# Revit family: HARMANN-Wentylator-Harmann-ML-EC-R_Wywiewny
name_source: partatom
category: Wyposażenie mechaniczne
units: mm (PartAtom-declared; Revit-internal decimal feet)

## family parameters
Oparty na płaszczyźnie roboczej = Nie
Punkt obliczania pomieszczeń = Nie
Tnij formami wycięć po wczytaniu = Nie
Typ części = Dzieli na
Współdzielony = Nie
Wymiar okrągłego złącza = Użyj średnicy
Zachowaj orientację opisów = Nie
Zawsze pionowo = Tak

## types (6) — shared parameters
Domyślna rzędna = 0.0 mm
IfcExportAs = IfcFanType
IfcExportType = NOTDEFINED
Kod Producent = Harmann
Kod Typoszereg = ML EC.R
Object Date = 2018.11.30
Object Destination = PL
Object ID = F000054RFAPL
Object Language = PL
Object Revit = 2017
Object Version = 1.00
Opis = Kanałowy wentylator  EC z wbudowanym potencjometrem
Otoczenie Temperatura Maksymalna = 50.0 °C
Otoczenie Temperatura Minimalna = -20.0 °C
Powietrze Wywiewane Temperatura Maksymalna = 50.0 °C
Producent = Harmann Polska Sp. z o.o.
Producent Nazwa = Harmann Polska Sp. z o.o.
Systematyka Branża = Instalacje Sanitarne
Systematyka Dziedzina = Instalacje Wentylacyjne
Systematyka Klasa = Wentylator
Systematyka Rodzaj = Wentylator Kanałowy
Zasilanie Częstotliwość Nominalna = 50 Hz
Zasilanie Ilość Faz = 1
Zasilanie Konfiguracja Uzwojeń = n/d
Zasilanie Napięcie Nominalne = 230 V
wx_a0 = 0.0 mm
wy_a0 = 53.9 mm

## per-type parameters (varying)
- ML EC.R 100/280: Kod Numer Katalogowy=01002801; Kod Zamówienia=ML EC.R 100/280; Masa Netto=2.0 kg; Model=ML EC.R 100/280; Opis indeksowy=ML EC.R 100/280; Otoczenie Poziom Ciśnienia Akustycznego Nominalny z 01 m=38; Otoczenie Poziom Ciśnienia Akustycznego Nominalny z 03 m=35; Otoczenie Poziom Mocy Akustycznej Nominalny Obudowa=42; Powietrze Wywiewane Ciśnienie Statyczne Maksymalne=160.0 Pa; Powietrze Wywiewane Ciśnienie Statyczne Nominalne=60.0 Pa; Powietrze Wywiewane Poziom Mocy Akustycznej Nominalny Wlot=52; Powietrze Wywiewane Poziom Mocy Akustycznej Nominalny Wylot=53; Powietrze Wywiewane Przepływ Maksymalny=280 m³/h; Powietrze Wywiewane Przepływ Nominalny=150 m³/h; Prt Komponent N1=GE-Komponent-ParaForma-Harmann-ML-N1a : ML EC.R 100/280; Prt Komponent N2=GE-Komponent-ParaForma-Harmann-ML-N2a : 100/280; Zasilanie Moc=20 W; Zasilanie Moc Pozorna=58 VA; Zasilanie Natężenie=0 A; Zasilanie Rodzaj Sterowania=Sterowanie napięciem 0-10V. Wbudowany potencjometr.; Zasilanie Współczynnik Mocy=0.35; dn=100.0 mm; l1_a0=119.0 mm; l2_a0=119.0 mm; s1=100.0 mm; wz_a0=88.5 mm
- ML EC.R 125/300: Kod Numer Katalogowy=01253001; Kod Zamówienia=ML EC.R 125/300; Masa Netto=1.8 kg; Model=ML EC.R 125/300; Opis indeksowy=ML EC.R 125/300; Otoczenie Poziom Ciśnienia Akustycznego Nominalny z 01 m=37; Otoczenie Poziom Ciśnienia Akustycznego Nominalny z 03 m=34; Otoczenie Poziom Mocy Akustycznej Nominalny Obudowa=41; Powietrze Wywiewane Ciśnienie Statyczne Maksymalne=140.0 Pa; Powietrze Wywiewane Ciśnienie Statyczne Nominalne=50.0 Pa; Powietrze Wywiewane Poziom Mocy Akustycznej Nominalny Wlot=55; Powietrze Wywiewane Poziom Mocy Akustycznej Nominalny Wylot=55; Powietrze Wywiewane Przepływ Maksymalny=300 m³/h; Powietrze Wywiewane Przepływ Nominalny=200 m³/h; Prt Komponent N1=GE-Komponent-ParaForma-Harmann-ML-N1a : ML EC.R 125/300; Prt Komponent N2=GE-Komponent-ParaForma-Harmann-ML-N2a : 125/300; Zasilanie Moc=18 W; Zasilanie Moc Pozorna=61 VA; Zasilanie Natężenie=0 A; Zasilanie Rodzaj Sterowania=Sterowanie napięciem 0-10V. Wbudowany potencjometr.; Zasilanie Współczynnik Mocy=0.21; dn=125.0 mm; l1_a0=99.5 mm; l2_a0=99.5 mm; s1=125.0 mm; wz_a0=88.5 mm
- ML EC.R 150-160/530: Kod Numer Katalogowy=01505301; Kod Zamówienia=ML EC.R 150-160/550; Masa Netto=2.7 kg; Model=ML EC.R 150-160/550; Opis indeksowy=ML EC.R 150-160/550; Otoczenie Poziom Ciśnienia Akustycznego Nominalny z 01 m=439; Otoczenie Poziom Ciśnienia Akustycznego Nominalny z 03 m=36; Otoczenie Poziom Mocy Akustycznej Nominalny Obudowa=43; Powietrze Wywiewane Ciśnienie Statyczne Maksymalne=350.0 Pa; Powietrze Wywiewane Ciśnienie Statyczne Nominalne=80.0 Pa; Powietrze Wywiewane Poziom Mocy Akustycznej Nominalny Wlot=55; Powietrze Wywiewane Poziom Mocy Akustycznej Nominalny Wylot=58; Powietrze Wywiewane Przepływ Maksymalny=530 m³/h; Powietrze Wywiewane Przepływ Nominalny=350 m³/h; Prt Komponent N1=GE-Komponent-ParaForma-Harmann-ML-N1a : ML EC.R 150-160/530; Prt Komponent N2=GE-Komponent-ParaForma-Harmann-ML-N2a : 150-160/530; Zasilanie Moc=50 W; Zasilanie Moc Pozorna=80 VA; Zasilanie Natężenie=0 A; Zasilanie Rodzaj Sterowania=Sterowanie napięciem 0-10V. Wbudowanz potencjometr; Zasilanie Współczynnik Mocy=0.62; dn=160.0 mm; l1_a0=145.0 mm; l2_a0=145.0 mm; s1=160.0 mm; wz_a0=99.5 mm
- ML EC.R 200/1150: Kod Numer Katalogowy=02001151; Kod Zamówienia=ML EC.R 200/950; Masa Netto=4.3 kg; Model=ML EC.R 200/950; Opis indeksowy=ML EC.R 200/950; Otoczenie Poziom Ciśnienia Akustycznego Nominalny z 01 m=44; Otoczenie Poziom Ciśnienia Akustycznego Nominalny z 03 m=41; Otoczenie Poziom Mocy Akustycznej Nominalny Obudowa=48; Powietrze Wywiewane Ciśnienie Statyczne Maksymalne=450.0 Pa; Powietrze Wywiewane Ciśnienie Statyczne Nominalne=100.0 Pa; Powietrze Wywiewane Poziom Mocy Akustycznej Nominalny Wlot=60; Powietrze Wywiewane Poziom Mocy Akustycznej Nominalny Wylot=62; Powietrze Wywiewane Przepływ Maksymalny=1100 m³/h; Powietrze Wywiewane Przepływ Nominalny=700 m³/h; Prt Komponent N1=GE-Komponent-ParaForma-Harmann-ML-N1a : ML EC.R 200/1150; Prt Komponent N2=GE-Komponent-ParaForma-Harmann-ML-N2a : 200/1150; Zasilanie Moc=165 W; Zasilanie Moc Pozorna=241 VA; Zasilanie Natężenie=1 A; Zasilanie Rodzaj Sterowania=Sterowanie napięciem 0-10V. Wbudowany potencjometr.; Zasilanie Współczynnik Mocy=0.68; dn=200.0 mm; l1_a0=120.0 mm; l2_a0=120.0 mm; s1=200.0 mm; wz_a0=111.0 mm
- ML EC.R 250/1650: Kod Numer Katalogowy=02501651; Kod Zamówienia=ML EC.R 250/1650; Masa Netto=6.5 kg; Model=ML EC.R 250/1650; Opis indeksowy=ML EC.R 250/1650; Otoczenie Poziom Ciśnienia Akustycznego Nominalny z 01 m=47; Otoczenie Poziom Ciśnienia Akustycznego Nominalny z 03 m=44; Otoczenie Poziom Mocy Akustycznej Nominalny Obudowa=51; Powietrze Wywiewane Ciśnienie Statyczne Maksymalne=600.0 Pa; Powietrze Wywiewane Ciśnienie Statyczne Nominalne=120.0 Pa; Powietrze Wywiewane Poziom Mocy Akustycznej Nominalny Wlot=59; Powietrze Wywiewane Poziom Mocy Akustycznej Nominalny Wylot=60; Powietrze Wywiewane Przepływ Maksymalny=1600 m³/h; Powietrze Wywiewane Przepływ Nominalny=900 m³/h; Prt Komponent N1=GE-Komponent-ParaForma-Harmann-ML-N1a : ML EC.R 250/1650; Prt Komponent N2=GE-Komponent-ParaForma-Harmann-ML-N2a : 250/1650; Zasilanie Moc=255 W; Zasilanie Moc Pozorna=614 VA; Zasilanie Natężenie=3 A; Zasilanie Rodzaj Sterowania=Sterowanie napięciem 0-10V. Wbudowany potencjometr.; Zasilanie Współczynnik Mocy=0.42; dn=250.0 mm; l1_a0=159.5 mm; l2_a0=159.5 mm; s1=250.0 mm; wz_a0=111.0 mm
- ML EC.R 315/2100: Kod Numer Katalogowy=03152101; Kod Zamówienia=ML EC.R 315/2100; Masa Netto=8.5 kg; Model=ML EC.R 315/2100; Opis indeksowy=ML EC.R 315/2100; Otoczenie Poziom Ciśnienia Akustycznego Nominalny z 01 m=50; Otoczenie Poziom Ciśnienia Akustycznego Nominalny z 03 m=47; Otoczenie Poziom Mocy Akustycznej Nominalny Obudowa=54; Powietrze Wywiewane Ciśnienie Statyczne Maksymalne=700.0 Pa; Powietrze Wywiewane Ciśnienie Statyczne Nominalne=150.0 Pa; Powietrze Wywiewane Poziom Mocy Akustycznej Nominalny Wlot=61; Powietrze Wywiewane Poziom Mocy Akustycznej Nominalny Wylot=64; Powietrze Wywiewane Przepływ Maksymalny=2100 m³/h; Powietrze Wywiewane Przepływ Nominalny=1000 m³/h; Prt Komponent N1=GE-Komponent-ParaForma-Harmann-ML-N1a : ML EC.R 315/2100; Prt Komponent N2=GE-Komponent-ParaForma-Harmann-ML-N2a : 315/2100; Zasilanie Moc=254 W; Zasilanie Moc Pozorna=621 VA; Zasilanie Natężenie=3 A; Zasilanie Rodzaj Sterowania=Sterowanie napięciem 0-10V. Wbudowany potencjometr.; Zasilanie Współczynnik Mocy=0.41; dn=315.0 mm; l1_a0=177.0 mm; l2_a0=177.0 mm; s1=315.0 mm; wz_a0=157.5 mm
